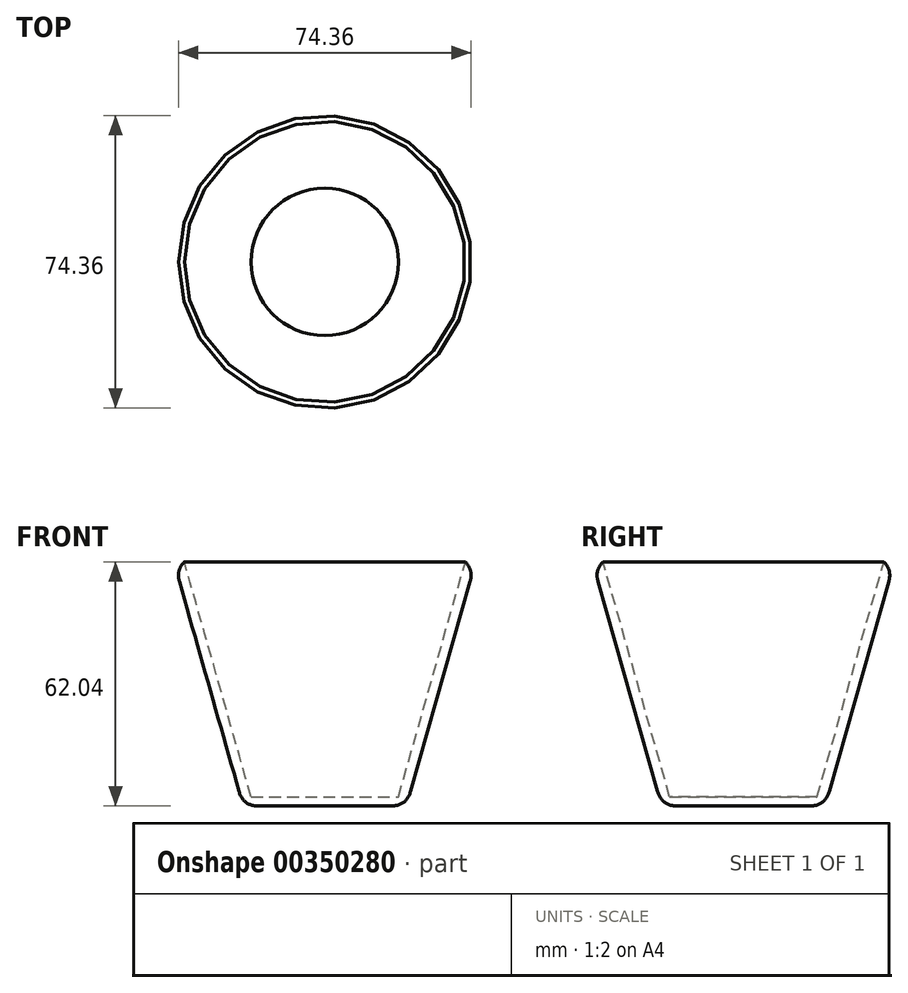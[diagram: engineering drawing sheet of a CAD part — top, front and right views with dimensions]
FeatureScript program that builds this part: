
annotation { "Feature Type Name" : "Feature", "Feature Type Description" : "" }
export const myFeature = defineFeature(function(context is Context, id is Id, definition is map)
    precondition{}
    {
        {
            var Q0;
            Q0=qCreatedBy(makeId("Front.planeOp"),FACE);
            var sketch = newSketch(context, id + "F0", { "sketchPlane" : qUnion([Q0])});
            skLineSegment(sketch, "E0", {"start": v(0, 0) * mm, "end": v(20.75, 0) * mm});
            skLineSegment(sketch, "E1", {"start": v(20.75, 0) * mm, "end": v(38.36, 62.04) * mm});
            skLineSegment(sketch, "E2", {"start": v(38.36, 62.04) * mm, "end": v(0, 62.04) * mm});
            skLineSegment(sketch, "E3", {"start": v(0, 8.71) * mm, "end": v(0, 62.04) * mm});
            skLineSegment(sketch, "E4", {"start": v(0, 0) * mm, "end": v(0, 8.71) * mm});
            skLineSegment(sketch, "E5", {"start": v(38.36, 62.04) * mm, "end": v(33.01, 62.04) * mm});
            skLineSegment(sketch, "E6", {"start": v(33.01, 62.04) * mm, "end": v(35.69, 62.04) * mm});
            skLineSegment(sketch, "E7", {"start": v(35.69, 62.04) * mm, "end": v(18.73, 2.32) * mm});
            skLineSegment(sketch, "E8", {"start": v(18.73, 2.32) * mm, "end": v(0, 2.32) * mm});
            skSolve(sketch);
        }
        {
            var Q0;
            {var subQ1=sQuery(id+"F0.wireOp",EDGE,"E0");Q0=makeQuery(id+"F0.imprint","IMPRINT",FACE,{"disambiguationData":[TD([[makeQuery(id+"F0.imprint","IMPRINT",EDGE,{"derivedFrom":subQ1}),1.0]])]});}
            var Q1;
            Q1=sQuery(id+"F0.wireOp",EDGE,"E3");
            revolve(context, id + "F1", {"entities" : qUnion([Q0]), "axis" : qUnion([Q1]), "revolveType" : RevolveType.FULL});
        }
        {
            var Q0;
            Q0=makeQuery(id+"F1.opRevolve","SWEPT_EDGE",EDGE,{"disambiguationData":[OSD([sQuery(id+"F0.wireOp",EDGE,"E1"),sQuery(id+"F0.wireOp",EDGE,"E5")])]});
            fillet(context, id + "F2", {"entities" : qUnion([Q0]), "radius" : 5.08 * mm, "tangentPropagation" : true, "rho" : 0.5, "crossSection" : FilletCrossSection.CONIC, "allowEdgeOverflow" : false});
        }
    });
